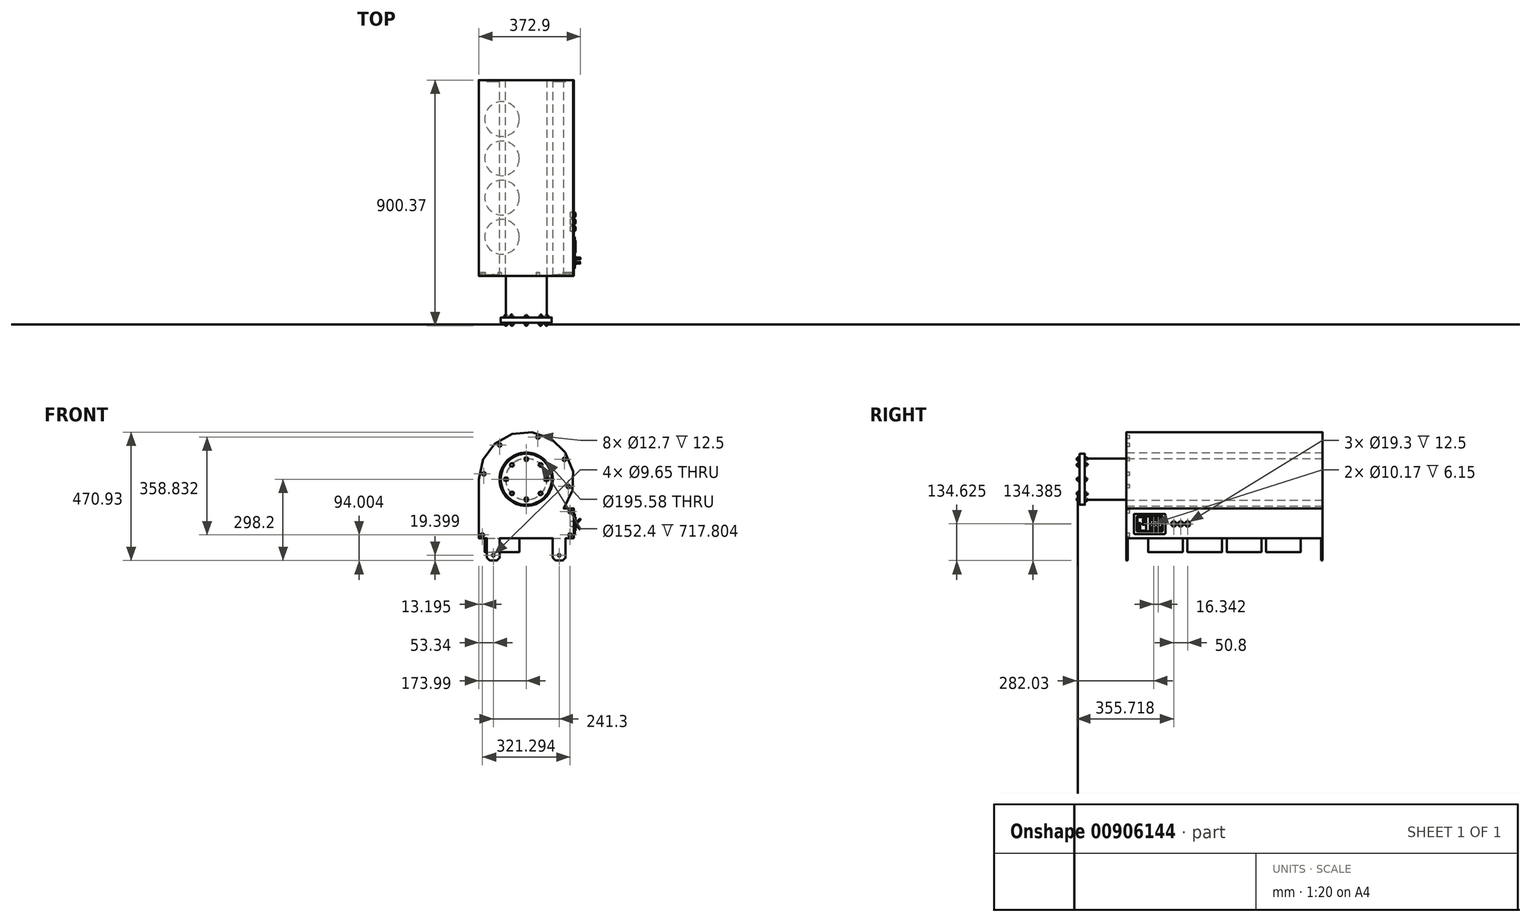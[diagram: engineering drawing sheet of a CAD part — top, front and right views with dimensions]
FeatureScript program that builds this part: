
annotation { "Feature Type Name" : "Feature", "Feature Type Description" : "" }
export const myFeature = defineFeature(function(context is Context, id is Id, definition is map)
    precondition{}
    {
        {
            var Q0;
            Q0=qCreatedBy(makeId("Front.planeOp"),FACE);
            var sketch = newSketch(context, id + "F0", { "sketchPlane" : qUnion([Q0])});
            skCircle(sketch, "E0", {"center": v(0, 0) * mm, "radius": 76.2 * mm});
            skCircle(sketch, "E1", {"center": v(0, 0) * mm, "radius": 97.8 * mm});
            skArc(sketch, "E2", {"start": v(137.14, -107.07) * mm, "mid": v(56.62, 164.52) * mm, "end": v(-174, 0) * mm});
            skLineSegment(sketch, "E3.top", {"start": v(-174, -216.3) * mm, "end": v(174, -216.3) * mm});
            skLineSegment(sketch, "E3.left", {"start": v(-174, -216.3) * mm, "end": v(-174, -216.3) * mm});
            skLineSegment(sketch, "E3.right", {"start": v(174, -107.07) * mm, "end": v(174, -216.3) * mm});
            skLineSegment(sketch, "E4", {"start": v(-174, 0) * mm, "end": v(-174, -216.3) * mm});
            skLineSegment(sketch, "E5.trimOffspring", {"start": v(137.14, -107.07) * mm, "end": v(174, -107.07) * mm});
            skLineSegment(sketch, "E6.bottom", {"start": v(96.9, -216.3) * mm, "end": v(144.4, -216.3) * mm});
            skLineSegment(sketch, "E6.top", {"start": v(96.9, -298.2) * mm, "end": v(144.4, -298.2) * mm});
            skLineSegment(sketch, "E6.left", {"start": v(96.9, -216.3) * mm, "end": v(96.9, -298.2) * mm});
            skLineSegment(sketch, "E6.right", {"start": v(144.4, -216.3) * mm, "end": v(144.4, -298.2) * mm});
            skLineSegment(sketch, "E7.bottom", {"start": v(-144.4, -216.3) * mm, "end": v(-96.9, -216.3) * mm});
            skLineSegment(sketch, "E7.top", {"start": v(-144.4, -298.2) * mm, "end": v(-96.9, -298.2) * mm});
            skLineSegment(sketch, "E7.left", {"start": v(-96.9, -216.3) * mm, "end": v(-96.9, -298.2) * mm});
            skLineSegment(sketch, "E7.right", {"start": v(-144.4, -216.3) * mm, "end": v(-144.4, -298.2) * mm});
            skCircle(sketch, "E8", {"center": v(-120.65, -278.8) * mm, "radius": 4.83 * mm});
            skPoint(sketch, "E8.centerSnap0", {"position": v(-120.65, -298.2) * mm});
            skCircle(sketch, "E9", {"center": v(120.65, -278.8) * mm, "radius": 4.83 * mm});
            skPoint(sketch, "E9.centerSnap0", {"position": v(120.65, -298.2) * mm});
            skSolve(sketch);
        }
        {
            var Q0;
            Q0=makeQuery(id+"F0.imprint","IMPRINT",FACE,{"disambiguationData":[TD([[makeQuery(id+"F0.imprint","IMPRINT",EDGE,{"derivedFrom":sQuery(id+"F0.wireOp",EDGE,"E1")}),-1.0]])]});
            extrude(context, id + "F1", {"entities" : qUnion([Q0]), "depth" : 717.8 * mm, "offsetDistance" : 25.4 * mm});
        }
        {
            var Q0;
            Q0=makeQuery(id+"F0.imprint","IMPRINT",FACE,{"disambiguationData":[TD([[makeQuery(id+"F0.imprint","IMPRINT",EDGE,{"derivedFrom":sQuery(id+"F0.wireOp",EDGE,"E0")}),-1.0]])]});
            extrude(context, id + "F2", {"entities" : qUnion([Q0]), "depth" : 717.8 * mm, "offsetDistance" : 25.4 * mm});
        }
        {
            var Q0;
            Q0=makeQuery(id+"F0.imprint","IMPRINT",FACE,{"disambiguationData":[TD([[makeQuery(id+"F0.imprint","IMPRINT",EDGE,{"derivedFrom":sQuery(id+"F0.wireOp",EDGE,"E7.top")}),1.0]])]});
            var Q1;
            Q1=makeQuery(id+"F0.imprint","IMPRINT",FACE,{"disambiguationData":[TD([[makeQuery(id+"F0.imprint","IMPRINT",EDGE,{"derivedFrom":sQuery(id+"F0.wireOp",EDGE,"E6.top")}),1.0]])]});
            extrude(context, id + "F3", {"entities" : qUnion([Q0, Q1]), "operationType" : NewBodyOperationType.ADD, "depth" : 5.08 * mm, "offsetDistance" : 25.4 * mm});
        }
        {
            var Q0;
            Q0=makeQuery(id+"F1.opExtrude","SWEPT_FACE",FACE,{"disambiguationData":[OSD([sQuery(id+"F0.wireOp",EDGE,"E3.top")])]});
            var sketch = newSketch(context, id + "F4", { "sketchPlane" : qUnion([Q0])});
            skCircle(sketch, "E10", {"center": v(-89.17, 143) * mm, "radius": 63.5 * mm});
            skCircle(sketch, "E11", {"center": v(-89.17, 286.94) * mm, "radius": 63.5 * mm});
            skCircle(sketch, "E12", {"center": v(-89.17, 430.87) * mm, "radius": 63.5 * mm});
            skCircle(sketch, "E13", {"center": v(-89.17, 574.8) * mm, "radius": 63.5 * mm});
            skLineSegment(sketch, "E14", {"start": v(-89.17, 0) * mm, "end": v(-89.17, 1107.64) * mm});
            skSolve(sketch);
        }
        {
            var Q0;
            {var subQ0=sQuery(id+"F4.wireOp",EDGE,"E14");var subQ1=sQuery(id+"F4.wireOp",EDGE,"E13");var subQ2=makeQuery(id+"F4.imprint","INTERSECT",VERTEX,{"disambiguationData":[OD(0.0)],"derivedFrom":[subQ1,subQ0]});Q0=makeQuery(id+"F4.imprint","IMPRINT",FACE,{"disambiguationData":[TD([[makeQuery(id+"F4.imprint","IMPRINT",EDGE,{"disambiguationData":[TD([[subQ2,-1.0]])],"derivedFrom":subQ1}),1.0]])]});}
            var Q1;
            {var subQ0=sQuery(id+"F4.wireOp",EDGE,"E14");var subQ1=sQuery(id+"F4.wireOp",EDGE,"E13");var subQ2=makeQuery(id+"F4.imprint","INTERSECT",VERTEX,{"disambiguationData":[OD(0.0)],"derivedFrom":[subQ1,subQ0]});Q1=makeQuery(id+"F4.imprint","IMPRINT",FACE,{"disambiguationData":[TD([[makeQuery(id+"F4.imprint","IMPRINT",EDGE,{"disambiguationData":[TD([[subQ2,1.0]])],"derivedFrom":subQ1}),1.0]])]});}
            var Q2;
            {var subQ0=sQuery(id+"F4.wireOp",EDGE,"E14");var subQ1=sQuery(id+"F4.wireOp",EDGE,"E12");var subQ2=makeQuery(id+"F4.imprint","INTERSECT",VERTEX,{"disambiguationData":[OD(0.0)],"derivedFrom":[subQ1,subQ0]});Q2=makeQuery(id+"F4.imprint","IMPRINT",FACE,{"disambiguationData":[TD([[makeQuery(id+"F4.imprint","IMPRINT",EDGE,{"disambiguationData":[TD([[subQ2,-1.0]])],"derivedFrom":subQ1}),1.0]])]});}
            var Q3;
            {var subQ0=sQuery(id+"F4.wireOp",EDGE,"E14");var subQ1=sQuery(id+"F4.wireOp",EDGE,"E12");var subQ2=makeQuery(id+"F4.imprint","INTERSECT",VERTEX,{"disambiguationData":[OD(0.0)],"derivedFrom":[subQ1,subQ0]});Q3=makeQuery(id+"F4.imprint","IMPRINT",FACE,{"disambiguationData":[TD([[makeQuery(id+"F4.imprint","IMPRINT",EDGE,{"disambiguationData":[TD([[subQ2,1.0]])],"derivedFrom":subQ1}),1.0]])]});}
            var Q4;
            {var subQ0=sQuery(id+"F4.wireOp",EDGE,"E14");var subQ1=sQuery(id+"F4.wireOp",EDGE,"E11");var subQ2=makeQuery(id+"F4.imprint","INTERSECT",VERTEX,{"disambiguationData":[OD(0.0)],"derivedFrom":[subQ1,subQ0]});Q4=makeQuery(id+"F4.imprint","IMPRINT",FACE,{"disambiguationData":[TD([[makeQuery(id+"F4.imprint","IMPRINT",EDGE,{"disambiguationData":[TD([[subQ2,-1.0]])],"derivedFrom":subQ1}),1.0]])]});}
            var Q5;
            {var subQ0=sQuery(id+"F4.wireOp",EDGE,"E14");var subQ1=sQuery(id+"F4.wireOp",EDGE,"E11");var subQ2=makeQuery(id+"F4.imprint","INTERSECT",VERTEX,{"disambiguationData":[OD(0.0)],"derivedFrom":[subQ1,subQ0]});Q5=makeQuery(id+"F4.imprint","IMPRINT",FACE,{"disambiguationData":[TD([[makeQuery(id+"F4.imprint","IMPRINT",EDGE,{"disambiguationData":[TD([[subQ2,1.0]])],"derivedFrom":subQ1}),1.0]])]});}
            var Q6;
            {var subQ0=sQuery(id+"F4.wireOp",EDGE,"E14");var subQ1=sQuery(id+"F4.wireOp",EDGE,"E10");var subQ2=makeQuery(id+"F4.imprint","INTERSECT",VERTEX,{"disambiguationData":[OD(0.0)],"derivedFrom":[subQ1,subQ0]});Q6=makeQuery(id+"F4.imprint","IMPRINT",FACE,{"disambiguationData":[TD([[makeQuery(id+"F4.imprint","IMPRINT",EDGE,{"disambiguationData":[TD([[subQ2,-1.0]])],"derivedFrom":subQ1}),1.0]])]});}
            var Q7;
            {var subQ0=sQuery(id+"F4.wireOp",EDGE,"E14");var subQ1=sQuery(id+"F4.wireOp",EDGE,"E10");var subQ2=makeQuery(id+"F4.imprint","INTERSECT",VERTEX,{"disambiguationData":[OD(0.0)],"derivedFrom":[subQ1,subQ0]});Q7=makeQuery(id+"F4.imprint","IMPRINT",FACE,{"disambiguationData":[TD([[makeQuery(id+"F4.imprint","IMPRINT",EDGE,{"disambiguationData":[TD([[subQ2,1.0]])],"derivedFrom":subQ1}),1.0]])]});}
            var Q8;
            Q8=makeQuery(id+"F1.opExtrude","SWEPT_FACE",FACE,{"disambiguationData":[OSD([sQuery(id+"F0.wireOp",EDGE,"E3.top")])]});
            extrude(context, id + "F5", {"entities" : qUnion([Q0, Q1, Q2, Q3, Q4, Q5, Q6, Q7]), "depth" : 50.8 * mm, "endBoundEntityFace" : qUnion([Q8]), "offsetDistance" : 127 * mm});
        }
        {
            var Q0;
            Q0=makeQuery(id+"F0.imprint","IMPRINT",FACE,{"disambiguationData":[TD([[makeQuery(id+"F0.imprint","IMPRINT",EDGE,{"derivedFrom":sQuery(id+"F0.wireOp",EDGE,"E6.top")}),1.0]])]});
            var Q1;
            Q1=makeQuery(id+"F0.imprint","IMPRINT",FACE,{"disambiguationData":[TD([[makeQuery(id+"F0.imprint","IMPRINT",EDGE,{"derivedFrom":sQuery(id+"F0.wireOp",EDGE,"E7.top")}),1.0]])]});
            extrude(context, id + "F6", {"entities" : qUnion([Q0, Q1]), "operationType" : NewBodyOperationType.ADD, "depth" : 717.8 * mm, "offsetDistance" : 25.4 * mm, "hasSecondDirection" : true, "secondDirectionOppositeDirection" : false, "secondDirectionDepth" : 712.72 * mm});
        }
        {
            var Q0;
            Q0=makeQuery(id+"F6.opExtrude","SWEPT_EDGE",EDGE,{"disambiguationData":[OSD([sQuery(id+"F0.wireOp",EDGE,"E6.top"),sQuery(id+"F0.wireOp",EDGE,"E6.right")])]});
            var Q1;
            Q1=makeQuery(id+"F6.opExtrude","SWEPT_EDGE",EDGE,{"disambiguationData":[OSD([sQuery(id+"F0.wireOp",EDGE,"E6.top"),sQuery(id+"F0.wireOp",EDGE,"E6.left")])]});
            var Q2;
            Q2=makeQuery(id+"F6.opExtrude","SWEPT_EDGE",EDGE,{"disambiguationData":[OSD([sQuery(id+"F0.wireOp",EDGE,"E3.top"),sQuery(id+"F0.wireOp",EDGE,"E6.right")])]});
            var Q3;
            Q3=makeQuery(id+"F6.opExtrude","SWEPT_EDGE",EDGE,{"disambiguationData":[OSD([sQuery(id+"F0.wireOp",EDGE,"E3.top"),sQuery(id+"F0.wireOp",EDGE,"E6.left")])]});
            var Q4;
            Q4=makeQuery(id+"F6.opExtrude","SWEPT_EDGE",EDGE,{"disambiguationData":[OSD([sQuery(id+"F0.wireOp",EDGE,"E3.top"),sQuery(id+"F0.wireOp",EDGE,"E7.right")])]});
            var Q5;
            Q5=makeQuery(id+"F6.opExtrude","SWEPT_EDGE",EDGE,{"disambiguationData":[OSD([sQuery(id+"F0.wireOp",EDGE,"E7.top"),sQuery(id+"F0.wireOp",EDGE,"E7.right")])]});
            var Q6;
            Q6=makeQuery(id+"F6.opExtrude","SWEPT_EDGE",EDGE,{"disambiguationData":[OSD([sQuery(id+"F0.wireOp",EDGE,"E7.top"),sQuery(id+"F0.wireOp",EDGE,"E7.left")])]});
            var Q7;
            Q7=makeQuery(id+"F6.opExtrude","SWEPT_EDGE",EDGE,{"disambiguationData":[OSD([sQuery(id+"F0.wireOp",EDGE,"E3.top"),sQuery(id+"F0.wireOp",EDGE,"E7.left")])]});
            var Q8;
            Q8=makeQuery(id+"F3.opExtrude","SWEPT_EDGE",EDGE,{"disambiguationData":[OSD([sQuery(id+"F0.wireOp",EDGE,"E7.top"),sQuery(id+"F0.wireOp",EDGE,"E7.right")])]});
            var Q9;
            Q9=makeQuery(id+"F3.opExtrude","SWEPT_EDGE",EDGE,{"disambiguationData":[OSD([sQuery(id+"F0.wireOp",EDGE,"E7.top"),sQuery(id+"F0.wireOp",EDGE,"E7.left")])]});
            var Q10;
            Q10=makeQuery(id+"F3.opExtrude","SWEPT_EDGE",EDGE,{"disambiguationData":[OSD([sQuery(id+"F0.wireOp",EDGE,"E3.top"),sQuery(id+"F0.wireOp",EDGE,"E7.right")])]});
            var Q11;
            Q11=makeQuery(id+"F3.opExtrude","SWEPT_EDGE",EDGE,{"disambiguationData":[OSD([sQuery(id+"F0.wireOp",EDGE,"E3.top"),sQuery(id+"F0.wireOp",EDGE,"E7.left")])]});
            var Q12;
            Q12=makeQuery(id+"F3.opExtrude","SWEPT_EDGE",EDGE,{"disambiguationData":[OSD([sQuery(id+"F0.wireOp",EDGE,"E6.top"),sQuery(id+"F0.wireOp",EDGE,"E6.left")])]});
            var Q13;
            Q13=makeQuery(id+"F3.opExtrude","SWEPT_EDGE",EDGE,{"disambiguationData":[OSD([sQuery(id+"F0.wireOp",EDGE,"E6.top"),sQuery(id+"F0.wireOp",EDGE,"E6.right")])]});
            var Q14;
            Q14=makeQuery(id+"F3.opExtrude","SWEPT_EDGE",EDGE,{"disambiguationData":[OSD([sQuery(id+"F0.wireOp",EDGE,"E3.top"),sQuery(id+"F0.wireOp",EDGE,"E6.right")])]});
            var Q15;
            Q15=makeQuery(id+"F3.opExtrude","SWEPT_EDGE",EDGE,{"disambiguationData":[OSD([sQuery(id+"F0.wireOp",EDGE,"E3.top"),sQuery(id+"F0.wireOp",EDGE,"E6.left")])]});
            chamfer(context, id + "F7", {"entities" : qUnion([Q0, Q1, Q2, Q3, Q4, Q5, Q6, Q7, Q8, Q9, Q10, Q11, Q12, Q13, Q14, Q15]), "width" : 10.16 * mm, "tangentPropagation" : true});
        }
        {
            var Q0;
            {var subQ0=sQuery(id+"F0.wireOp",EDGE,"E3.top");Q0=makeQuery(id+"F6.boolean.opBoolean","MERGE",FACE,{"derivedFrom":[makeQuery(id+"F1.opExtrude","CAP_FACE",FACE,{"disambiguationData":[OSD([sQuery(id+"F0.wireOp",EDGE,"E1"),sQuery(id+"F0.wireOp",EDGE,"E2"),subQ0,sQuery(id+"F0.wireOp",EDGE,"E3.right"),sQuery(id+"F0.wireOp",EDGE,"E4"),sQuery(id+"F0.wireOp",EDGE,"E5.trimOffspring")])],"isStart":false}),makeQuery(id+"F6.opExtrude","CAP_FACE",FACE,{"disambiguationData":[OSD([subQ0,sQuery(id+"F0.wireOp",EDGE,"E7.top"),sQuery(id+"F0.wireOp",EDGE,"E7.left"),sQuery(id+"F0.wireOp",EDGE,"E7.right"),sQuery(id+"F0.wireOp",EDGE,"E8")])],"isStart":false}),makeQuery(id+"F6.opExtrude","CAP_FACE",FACE,{"disambiguationData":[OSD([subQ0,sQuery(id+"F0.wireOp",EDGE,"E6.top"),sQuery(id+"F0.wireOp",EDGE,"E6.left"),sQuery(id+"F0.wireOp",EDGE,"E6.right"),sQuery(id+"F0.wireOp",EDGE,"E9")])],"isStart":false})]});}
            var sketch = newSketch(context, id + "F8", { "sketchPlane" : qUnion([Q0])});
            skCircle(sketch, "E15", {"center": v(0, 0) * mm, "radius": 75.2 * mm});
            skSolve(sketch);
        }
        {
            var Q0;
            Q0 = qSketchRegion(id + "F8", true);
            extrude(context, id + "F9", {"entities" : qUnion([Q0]), "depth" : 152.4 * mm, "offsetDistance" : 25.4 * mm});
        }
        {
            var Q0;
            Q0=makeQuery(id+"F9.opExtrude","CAP_FACE",FACE,{"disambiguationData":[OSD([sQuery(id+"F8.wireOp",EDGE,"E15")])],"isStart":false});
            var sketch = newSketch(context, id + "F10", { "sketchPlane" : qUnion([Q0])});
            skCircle(sketch, "E16", {"center": v(0, 0) * mm, "radius": 93.36 * mm});
            skSolve(sketch);
        }
        {
            var Q0;
            Q0 = qSketchRegion(id + "F10", true);
            extrude(context, id + "F11", {"entities" : qUnion([Q0]), "operationType" : NewBodyOperationType.ADD, "depth" : 19.05 * mm, "offsetDistance" : 25.4 * mm});
        }
        {
            var Q0;
            Q0=makeQuery(id+"F11.opExtrude","CAP_FACE",FACE,{"disambiguationData":[OSD([sQuery(id+"F10.wireOp",EDGE,"E16")])],"isStart":false});
            var sketch = newSketch(context, id + "F12", { "sketchPlane" : qUnion([Q0])});
            skLineSegment(sketch, "E17", {"start": v(0, 0) * mm, "end": v(0, 93.36) * mm, "construction": true});
            skCircle(sketch, "E18.cCircle", {"center": v(0, 74.1) * mm, "radius": 6.35 * mm, "construction": true});
            skLineSegment(sketch, "E18.0", {"start": v(6.35, 77.76) * mm, "end": v(6.35, 70.43) * mm});
            skLineSegment(sketch, "E18.1", {"start": v(6.35, 70.43) * mm, "end": v(0, 66.76) * mm});
            skLineSegment(sketch, "E18.2", {"start": v(0, 66.76) * mm, "end": v(-6.35, 70.43) * mm});
            skLineSegment(sketch, "E18.3", {"start": v(-6.35, 70.43) * mm, "end": v(-6.35, 77.76) * mm});
            skLineSegment(sketch, "E18.4", {"start": v(-6.35, 77.76) * mm, "end": v(0, 81.43) * mm});
            skLineSegment(sketch, "E18.5", {"start": v(0, 81.43) * mm, "end": v(6.35, 77.76) * mm});
            skPoint(sketch, "E18.0.midPoint", {"position": v(6.35, 74.1) * mm});
            skSolve(sketch);
        }
        {
            var Q0;
            Q0 = qSketchRegion(id + "F12", true);
            extrude(context, id + "F13", {"entities" : qUnion([Q0]), "depth" : 6.35 * mm, "offsetDistance" : 25.4 * mm});
        }
        {
            var Q0;
            Q0=makeQuery(id+"F13.opExtrude","CAP_FACE",FACE,{"disambiguationData":[OSD([sQuery(id+"F12.wireOp",EDGE,"E18.0"),sQuery(id+"F12.wireOp",EDGE,"E18.1"),sQuery(id+"F12.wireOp",EDGE,"E18.2"),sQuery(id+"F12.wireOp",EDGE,"E18.3"),sQuery(id+"F12.wireOp",EDGE,"E18.4"),sQuery(id+"F12.wireOp",EDGE,"E18.5")])],"isStart":false});
            var sketch = newSketch(context, id + "F14", { "sketchPlane" : qUnion([Q0])});
            skCircle(sketch, "E19", {"center": v(0, 74.1) * mm, "radius": 4.76 * mm});
            skSolve(sketch);
        }
        {
            var Q0;
            Q0 = qSketchRegion(id + "F14", true);
            extrude(context, id + "F15", {"entities" : qUnion([Q0]), "operationType" : NewBodyOperationType.ADD, "depth" : 4.76 * mm, "offsetDistance" : 25.4 * mm});
        }
        {
            var Q0;
            Q0=makeQuery(id+"F15.opExtrude","CAP_FACE",FACE,{"disambiguationData":[OSD([sQuery(id+"F14.wireOp",EDGE,"E19")])],"isStart":false});
            fillet(context, id + "F16", {"entities" : qUnion([Q0]), "radius" : 4.76 * mm, "tangentPropagation" : true, "rho" : 0.5, "crossSection" : FilletCrossSection.CONIC, "allowEdgeOverflow" : false});
        }
        {
            var Q0;
            Q0=makeQuery(id+"F11.opExtrude","CAP_EDGE",EDGE,{"disambiguationData":[OSD([sQuery(id+"F10.wireOp",EDGE,"E16")])],"isStart":false});
            var Q1;
            Q1=makeQuery(id+"F11.opExtrude","CAP_EDGE",EDGE,{"disambiguationData":[OSD([sQuery(id+"F10.wireOp",EDGE,"E16")])],"isStart":true});
            fillet(context, id + "F17", {"entities" : qUnion([Q0, Q1]), "radius" : 0.2 * mm, "tangentPropagation" : true, "allowEdgeOverflow" : false});
        }
        {
            var Q0;
            Q0=makeQuery(id+"F12.imprint","IMPRINT",FACE,{"disambiguationData":[TD([[makeQuery(id+"F12.imprint","IMPRINT",EDGE,{"derivedFrom":sQuery(id+"F12.wireOp",EDGE,"E18.0")}),1.0]])]});
            var Q1;
            Q1=makeQuery(id+"F11.opExtrude","CAP_FACE",FACE,{"disambiguationData":[OSD([sQuery(id+"F10.wireOp",EDGE,"E16")])],"isStart":true});
            cPlane(context, id + "F18", {"entities" : qUnion([Q0, Q1]), "cplaneType" : CPlaneType.MID_PLANE, "offset" : 25.4 * mm, "width" : 152.4 * mm, "height" : 152.4 * mm});
        }
        {
            var Q0;
            Q0=makeQuery(id+"F13.opExtrude","SWEPT_BODY",BODY,{"disambiguationData":[OSD([sQuery(id+"F12.wireOp",EDGE,"E18.0"),sQuery(id+"F12.wireOp",EDGE,"E18.1"),sQuery(id+"F12.wireOp",EDGE,"E18.2"),sQuery(id+"F12.wireOp",EDGE,"E18.3"),sQuery(id+"F12.wireOp",EDGE,"E18.4"),sQuery(id+"F12.wireOp",EDGE,"E18.5")])]});
            var Q1;
            Q1=qCreatedBy(id+"F18.planeOp",FACE);
            mirror(context, id + "F19", {"entities" : qUnion([Q0]), "mirrorPlane" : qUnion([Q1])});
        }
        {
            var Q0;
            Q0=sQuery(id+"F12.wireOp",EDGE,"E17");
            cPlane(context, id + "F20", {"entities" : qUnion([Q0]), "cplaneType" : CPlaneType.LINE_ANGLE, "offset" : 25.4 * mm, "angle" : 0 * degree, "width" : 152.4 * mm, "height" : 152.4 * mm});
        }
        {
            var Q0;
            Q0=qCreatedBy(id+"F20.planeOp",FACE);
            var sketch = newSketch(context, id + "F21", { "sketchPlane" : qUnion([Q0])});
            skLineSegment(sketch, "E20", {"start": v(-905.59, 0) * mm, "end": v(-759.23, 0) * mm, "construction": true});
            skSolve(sketch);
        }
        {
            var Q0;
            Q0=makeQuery(id+"F13.opExtrude","SWEPT_BODY",BODY,{"disambiguationData":[OSD([sQuery(id+"F12.wireOp",EDGE,"E18.0"),sQuery(id+"F12.wireOp",EDGE,"E18.1"),sQuery(id+"F12.wireOp",EDGE,"E18.2"),sQuery(id+"F12.wireOp",EDGE,"E18.3"),sQuery(id+"F12.wireOp",EDGE,"E18.4"),sQuery(id+"F12.wireOp",EDGE,"E18.5")])]});
            var Q1;
            Q1=makeQuery(id+"F19.opPattern","COPY",BODY,{"derivedFrom":makeQuery(id+"F13.opExtrude","SWEPT_BODY",BODY,{"disambiguationData":[OSD([sQuery(id+"F12.wireOp",EDGE,"E18.0"),sQuery(id+"F12.wireOp",EDGE,"E18.1"),sQuery(id+"F12.wireOp",EDGE,"E18.2"),sQuery(id+"F12.wireOp",EDGE,"E18.3"),sQuery(id+"F12.wireOp",EDGE,"E18.4"),sQuery(id+"F12.wireOp",EDGE,"E18.5")])]}),"instanceName":"1"});
            var Q2;
            Q2=sQuery(id+"F21.wireOp",EDGE,"E20");
            circularPattern(context, id + "F22", {"entities" : qUnion([Q0, Q1]), "axis" : qUnion([Q2]), "angle" : 360 * degree, "instanceCount" : 8, "equalSpace" : true});
        }
        {
            var Q0;
            Q0=makeQuery(id+"F1.opExtrude","SWEPT_FACE",FACE,{"disambiguationData":[OSD([sQuery(id+"F0.wireOp",EDGE,"E3.right")])]});
            var sketch = newSketch(context, id + "F23", { "sketchPlane" : qUnion([Q0])});
            skLineSegment(sketch, "E21.bottom", {"start": v(-678.44, -136.9) * mm, "end": v(-587.4, -136.9) * mm});
            skLineSegment(sketch, "E21.top", {"start": v(-678.44, -190.72) * mm, "end": v(-587.4, -190.72) * mm});
            skLineSegment(sketch, "E21.left", {"start": v(-680.44, -138.9) * mm, "end": v(-680.44, -188.72) * mm});
            skLineSegment(sketch, "E21.right", {"start": v(-585.4, -138.9) * mm, "end": v(-585.4, -188.72) * mm});
            skLineSegment(sketch, "E22", {"start": v(-680.44, -190.72) * mm, "end": v(-585.4, -136.9) * mm, "construction": true});
            skLineSegment(sketch, "E23.bottom", {"start": v(-687.44, -126.9) * mm, "end": v(-578.4, -126.9) * mm});
            skLineSegment(sketch, "E23.top", {"start": v(-687.44, -200.72) * mm, "end": v(-578.4, -200.72) * mm});
            skLineSegment(sketch, "E23.left", {"start": v(-690.44, -129.9) * mm, "end": v(-690.44, -197.72) * mm});
            skLineSegment(sketch, "E23.right", {"start": v(-575.4, -129.9) * mm, "end": v(-575.4, -197.72) * mm});
            skLineSegment(sketch, "E24", {"start": v(-632.92, -190.72) * mm, "end": v(-632.92, -200.72) * mm, "construction": true});
            skLineSegment(sketch, "E25", {"start": v(-575.4, -163.81) * mm, "end": v(-585.4, -163.81) * mm, "construction": true});
            skPoint(sketch, "E26.visualSharp", {"position": v(-680.44, -136.9) * mm});
            skArc(sketch, "E26.filletArc", {"start": v(-678.44, -136.9) * mm, "mid": v(-679.86, -137.5) * mm, "end": v(-680.44, -138.9) * mm});
            skPoint(sketch, "E27.visualSharp", {"position": v(-585.4, -136.9) * mm});
            skArc(sketch, "E27.filletArc", {"start": v(-585.4, -138.9) * mm, "mid": v(-585.99, -137.5) * mm, "end": v(-587.4, -136.9) * mm});
            skPoint(sketch, "E28.visualSharp", {"position": v(-585.4, -190.72) * mm});
            skArc(sketch, "E28.filletArc", {"start": v(-587.4, -190.72) * mm, "mid": v(-585.99, -190.14) * mm, "end": v(-585.4, -188.72) * mm});
            skPoint(sketch, "E29.visualSharp", {"position": v(-680.44, -190.72) * mm});
            skArc(sketch, "E29.filletArc", {"start": v(-680.44, -188.72) * mm, "mid": v(-679.86, -190.14) * mm, "end": v(-678.44, -190.72) * mm});
            skPoint(sketch, "E30.visualSharp", {"position": v(-690.44, -126.9) * mm});
            skArc(sketch, "E30.filletArc", {"start": v(-687.44, -126.9) * mm, "mid": v(-689.56, -127.78) * mm, "end": v(-690.44, -129.9) * mm});
            skPoint(sketch, "E31.visualSharp", {"position": v(-575.4, -126.9) * mm});
            skArc(sketch, "E31.filletArc", {"start": v(-575.4, -129.9) * mm, "mid": v(-576.28, -127.78) * mm, "end": v(-578.4, -126.9) * mm});
            skPoint(sketch, "E32.visualSharp", {"position": v(-575.4, -200.72) * mm});
            skArc(sketch, "E32.filletArc", {"start": v(-578.4, -200.72) * mm, "mid": v(-576.28, -199.85) * mm, "end": v(-575.4, -197.72) * mm});
            skPoint(sketch, "E33.visualSharp", {"position": v(-690.44, -200.72) * mm});
            skArc(sketch, "E33.filletArc", {"start": v(-690.44, -197.72) * mm, "mid": v(-689.56, -199.85) * mm, "end": v(-687.44, -200.72) * mm});
            skSolve(sketch);
        }
        {
            var Q0;
            Q0 = qSketchRegion(id + "F23", true);
            extrude(context, id + "F24", {"entities" : qUnion([Q0]), "depth" : 4 * mm, "offsetDistance" : 25.4 * mm});
        }
        {
            var Q0;
            Q0=makeQuery(id+"F24.opExtrude","CAP_FACE",FACE,{"disambiguationData":[OSD([sQuery(id+"F23.wireOp",EDGE,"E21.bottom"),sQuery(id+"F23.wireOp",EDGE,"E21.top"),sQuery(id+"F23.wireOp",EDGE,"E21.left"),sQuery(id+"F23.wireOp",EDGE,"E21.right"),sQuery(id+"F23.wireOp",EDGE,"E23.bottom"),sQuery(id+"F23.wireOp",EDGE,"E23.top"),sQuery(id+"F23.wireOp",EDGE,"E23.left"),sQuery(id+"F23.wireOp",EDGE,"E23.right"),sQuery(id+"F23.wireOp",EDGE,"E26.filletArc"),sQuery(id+"F23.wireOp",EDGE,"E27.filletArc"),sQuery(id+"F23.wireOp",EDGE,"E28.filletArc"),sQuery(id+"F23.wireOp",EDGE,"E29.filletArc"),sQuery(id+"F23.wireOp",EDGE,"E30.filletArc"),sQuery(id+"F23.wireOp",EDGE,"E31.filletArc"),sQuery(id+"F23.wireOp",EDGE,"E32.filletArc"),sQuery(id+"F23.wireOp",EDGE,"E33.filletArc")])],"isStart":false});
            fillet(context, id + "F25", {"entities" : qUnion([Q0]), "radius" : 1 * mm, "tangentPropagation" : true, "allowEdgeOverflow" : false});
        }
        {
            var Q0;
            {var subQ0=sQuery(id+"F0.wireOp",EDGE,"E3.top");Q0=makeQuery(id+"F6.boolean.opBoolean","MERGE",FACE,{"derivedFrom":[makeQuery(id+"F1.opExtrude","CAP_FACE",FACE,{"disambiguationData":[OSD([sQuery(id+"F0.wireOp",EDGE,"E1"),sQuery(id+"F0.wireOp",EDGE,"E2"),subQ0,sQuery(id+"F0.wireOp",EDGE,"E3.right"),sQuery(id+"F0.wireOp",EDGE,"E4"),sQuery(id+"F0.wireOp",EDGE,"E5.trimOffspring")])],"isStart":false}),makeQuery(id+"F6.opExtrude","CAP_FACE",FACE,{"disambiguationData":[OSD([subQ0,sQuery(id+"F0.wireOp",EDGE,"E7.top"),sQuery(id+"F0.wireOp",EDGE,"E7.left"),sQuery(id+"F0.wireOp",EDGE,"E7.right"),sQuery(id+"F0.wireOp",EDGE,"E8")])],"isStart":false}),makeQuery(id+"F6.opExtrude","CAP_FACE",FACE,{"disambiguationData":[OSD([subQ0,sQuery(id+"F0.wireOp",EDGE,"E6.top"),sQuery(id+"F0.wireOp",EDGE,"E6.left"),sQuery(id+"F0.wireOp",EDGE,"E6.right"),sQuery(id+"F0.wireOp",EDGE,"E9")])],"isStart":false})]});}
            var sketch = newSketch(context, id + "F26", { "sketchPlane" : qUnion([Q0])});
            skCircle(sketch, "E34", {"center": v(-97.37, 125.44) * mm, "radius": 6.35 * mm});
            skCircle(sketch, "E35", {"center": v(42.68, 154.64) * mm, "radius": 6.35 * mm});
            skCircle(sketch, "E36", {"center": v(139.9, 72.94) * mm, "radius": 6.35 * mm});
            skCircle(sketch, "E37", {"center": v(-155.38, 19.68) * mm, "radius": 6.35 * mm});
            skCircle(sketch, "E38", {"center": v(-160.8, -204.2) * mm, "radius": 6.35 * mm});
            skCircle(sketch, "E39", {"center": v(160.5, -204.2) * mm, "radius": 6.35 * mm});
            skCircle(sketch, "E40", {"center": v(160.5, -118.6) * mm, "radius": 6.35 * mm});
            skCircle(sketch, "E41", {"center": v(154.01, -26.43) * mm, "radius": 6.35 * mm});
            skSolve(sketch);
        }
        {
            var Q0;
            Q0 = qSketchRegion(id + "F26", true);
            extrude(context, id + "F27", {"entities" : qUnion([Q0]), "operationType" : NewBodyOperationType.REMOVE, "oppositeDirection" : true, "depth" : 12.7 * mm, "offsetDistance" : 25.4 * mm});
        }
        {
            var Q0;
            {var subQ0=sQuery(id+"F0.wireOp",EDGE,"E3.top");Q0=makeQuery(id+"F6.boolean.opBoolean","MERGE",FACE,{"derivedFrom":[makeQuery(id+"F1.opExtrude","CAP_FACE",FACE,{"disambiguationData":[OSD([sQuery(id+"F0.wireOp",EDGE,"E1"),sQuery(id+"F0.wireOp",EDGE,"E2"),subQ0,sQuery(id+"F0.wireOp",EDGE,"E3.right"),sQuery(id+"F0.wireOp",EDGE,"E4"),sQuery(id+"F0.wireOp",EDGE,"E5.trimOffspring")])],"isStart":false}),makeQuery(id+"F6.opExtrude","CAP_FACE",FACE,{"disambiguationData":[OSD([subQ0,sQuery(id+"F0.wireOp",EDGE,"E7.top"),sQuery(id+"F0.wireOp",EDGE,"E7.left"),sQuery(id+"F0.wireOp",EDGE,"E7.right"),sQuery(id+"F0.wireOp",EDGE,"E8")])],"isStart":false}),makeQuery(id+"F6.opExtrude","CAP_FACE",FACE,{"disambiguationData":[OSD([subQ0,sQuery(id+"F0.wireOp",EDGE,"E6.top"),sQuery(id+"F0.wireOp",EDGE,"E6.left"),sQuery(id+"F0.wireOp",EDGE,"E6.right"),sQuery(id+"F0.wireOp",EDGE,"E9")])],"isStart":false})]});}
            var sketch = newSketch(context, id + "F28", { "sketchPlane" : qUnion([Q0])});
            skCircle(sketch, "E42", {"center": v(-160.8, -204.2) * mm, "radius": 5.72 * mm});
            skCircle(sketch, "E43", {"center": v(-155.38, 19.68) * mm, "radius": 5.72 * mm});
            skCircle(sketch, "E44", {"center": v(-97.37, 125.44) * mm, "radius": 5.72 * mm});
            skCircle(sketch, "E45", {"center": v(42.68, 154.64) * mm, "radius": 5.72 * mm});
            skCircle(sketch, "E46", {"center": v(139.9, 72.94) * mm, "radius": 5.72 * mm});
            skCircle(sketch, "E47", {"center": v(154.01, -26.43) * mm, "radius": 5.72 * mm});
            skCircle(sketch, "E48", {"center": v(160.5, -118.6) * mm, "radius": 5.72 * mm});
            skCircle(sketch, "E49", {"center": v(160.5, -204.2) * mm, "radius": 5.72 * mm});
            skSolve(sketch);
        }
        {
            var Q0;
            Q0 = qSketchRegion(id + "F28", true);
            extrude(context, id + "F29", {"entities" : qUnion([Q0]), "oppositeDirection" : true, "depth" : 11.43 * mm, "offsetDistance" : 25.4 * mm});
        }
        {
            var Q0;
            Q0=makeQuery(id+"F1.opExtrude","SWEPT_FACE",FACE,{"disambiguationData":[OSD([sQuery(id+"F0.wireOp",EDGE,"E3.right")])]});
            var sketch = newSketch(context, id + "F30", { "sketchPlane" : qUnion([Q0])});
            skLineSegment(sketch, "E50.bottom", {"start": v(-677.9, -139.44) * mm, "end": v(-646.15, -139.44) * mm});
            skLineSegment(sketch, "E50.top", {"start": v(-677.9, -188.18) * mm, "end": v(-646.15, -188.18) * mm});
            skLineSegment(sketch, "E50.left", {"start": v(-677.9, -139.44) * mm, "end": v(-677.9, -188.18) * mm});
            skLineSegment(sketch, "E50.right", {"start": v(-646.15, -139.44) * mm, "end": v(-646.15, -188.18) * mm});
            skLineSegment(sketch, "E51.bottom", {"start": v(-632.4, -139.44) * mm, "end": v(-587.94, -139.44) * mm});
            skLineSegment(sketch, "E51.top", {"start": v(-632.4, -188.18) * mm, "end": v(-587.94, -188.18) * mm});
            skLineSegment(sketch, "E51.left", {"start": v(-632.4, -139.44) * mm, "end": v(-632.4, -188.18) * mm});
            skLineSegment(sketch, "E51.right", {"start": v(-587.94, -139.44) * mm, "end": v(-587.94, -188.18) * mm});
            skLineSegment(sketch, "E52.bottom", {"start": v(-627.46, -141.9) * mm, "end": v(-619.72, -141.9) * mm});
            skLineSegment(sketch, "E52.top", {"start": v(-627.46, -150.67) * mm, "end": v(-619.72, -150.67) * mm});
            skLineSegment(sketch, "E52.left", {"start": v(-627.46, -141.9) * mm, "end": v(-627.46, -150.67) * mm});
            skLineSegment(sketch, "E52.right", {"start": v(-619.72, -141.9) * mm, "end": v(-619.72, -150.67) * mm});
            skLineSegment(sketch, "E53.bottom", {"start": v(-613.7, -141.9) * mm, "end": v(-605.95, -141.9) * mm});
            skLineSegment(sketch, "E53.top", {"start": v(-613.7, -150.67) * mm, "end": v(-605.95, -150.67) * mm});
            skLineSegment(sketch, "E53.left", {"start": v(-613.7, -141.9) * mm, "end": v(-613.7, -150.67) * mm});
            skLineSegment(sketch, "E53.right", {"start": v(-605.95, -141.9) * mm, "end": v(-605.95, -150.67) * mm});
            skLineSegment(sketch, "E54.bottom", {"start": v(-600.28, -141.9) * mm, "end": v(-592.54, -141.9) * mm});
            skLineSegment(sketch, "E54.top", {"start": v(-600.28, -150.67) * mm, "end": v(-592.54, -150.67) * mm});
            skLineSegment(sketch, "E54.left", {"start": v(-600.28, -141.9) * mm, "end": v(-600.28, -150.67) * mm});
            skLineSegment(sketch, "E54.right", {"start": v(-592.54, -141.9) * mm, "end": v(-592.54, -150.67) * mm});
            skLineSegment(sketch, "E55.bottom", {"start": v(-627.46, -176.13) * mm, "end": v(-619.72, -176.13) * mm});
            skLineSegment(sketch, "E55.top", {"start": v(-627.46, -184.9) * mm, "end": v(-619.72, -184.9) * mm});
            skLineSegment(sketch, "E55.left", {"start": v(-627.46, -176.13) * mm, "end": v(-627.46, -184.9) * mm});
            skLineSegment(sketch, "E55.right", {"start": v(-619.72, -176.13) * mm, "end": v(-619.72, -184.9) * mm});
            skLineSegment(sketch, "E56.bottom", {"start": v(-613.7, -176.13) * mm, "end": v(-605.95, -176.13) * mm});
            skLineSegment(sketch, "E56.top", {"start": v(-613.7, -184.9) * mm, "end": v(-605.95, -184.9) * mm});
            skLineSegment(sketch, "E56.left", {"start": v(-613.7, -176.13) * mm, "end": v(-613.7, -184.9) * mm});
            skLineSegment(sketch, "E56.right", {"start": v(-605.95, -176.13) * mm, "end": v(-605.95, -184.9) * mm});
            skLineSegment(sketch, "E57.bottom", {"start": v(-600.28, -176.13) * mm, "end": v(-592.54, -176.13) * mm});
            skLineSegment(sketch, "E57.top", {"start": v(-600.28, -184.9) * mm, "end": v(-592.54, -184.9) * mm});
            skLineSegment(sketch, "E57.left", {"start": v(-600.28, -176.13) * mm, "end": v(-600.28, -184.9) * mm});
            skLineSegment(sketch, "E57.right", {"start": v(-592.54, -176.13) * mm, "end": v(-592.54, -184.9) * mm});
            skCircle(sketch, "E58", {"center": v(-618.34, -163.57) * mm, "radius": 5.09 * mm});
            skCircle(sketch, "E59", {"center": v(-602, -163.57) * mm, "radius": 5.09 * mm});
            skLineSegment(sketch, "E60.bottom", {"start": v(-673.14, -160.52) * mm, "end": v(-666.79, -160.52) * mm});
            skLineSegment(sketch, "E60.top", {"start": v(-673.14, -166.87) * mm, "end": v(-666.79, -166.87) * mm});
            skLineSegment(sketch, "E60.left", {"start": v(-673.14, -160.52) * mm, "end": v(-673.14, -166.87) * mm});
            skLineSegment(sketch, "E60.right", {"start": v(-666.79, -160.52) * mm, "end": v(-666.79, -166.87) * mm});
            skLineSegment(sketch, "E61.bottom", {"start": v(-657.26, -160.57) * mm, "end": v(-650.91, -160.57) * mm});
            skLineSegment(sketch, "E61.top", {"start": v(-657.26, -166.92) * mm, "end": v(-650.91, -166.92) * mm});
            skLineSegment(sketch, "E61.left", {"start": v(-657.26, -160.57) * mm, "end": v(-657.26, -166.92) * mm});
            skLineSegment(sketch, "E61.right", {"start": v(-650.91, -160.57) * mm, "end": v(-650.91, -166.92) * mm});
            skPoint(sketch, "E62", {"position": v(-646.15, -163.81) * mm});
            skPoint(sketch, "E63", {"position": v(-650.91, -163.75) * mm});
            skPoint(sketch, "E64", {"position": v(-666.79, -163.7) * mm});
            skPoint(sketch, "E65", {"position": v(-657.26, -163.75) * mm});
            skPoint(sketch, "E66", {"position": v(-662.03, -139.44) * mm});
            skLineSegment(sketch, "E67", {"start": v(-666.79, -163.7) * mm, "end": v(-657.26, -163.75) * mm, "construction": true});
            skPoint(sketch, "E68", {"position": v(-662.03, -163.72) * mm});
            skSolve(sketch);
        }
        {
            var Q0;
            Q0 = qSketchRegion(id + "F30", true);
            extrude(context, id + "F31", {"entities" : qUnion([Q0]), "operationType" : NewBodyOperationType.ADD, "depth" : 6.35 * mm, "offsetDistance" : 25.4 * mm});
        }
        {
            var Q0;
            Q0=makeQuery(id+"F31.opExtrude","SWEPT_FACE",FACE,{"disambiguationData":[OSD([sQuery(id+"F30.wireOp",EDGE,"E60.right")])]});
            cPlane(context, id + "F32", {"entities" : qUnion([Q0]), "cplaneType" : CPlaneType.OFFSET, "offset" : 0.25 * mm, "width" : 152.4 * mm, "height" : 152.4 * mm});
        }
        {
            var Q0;
            Q0=qCreatedBy(id+"F32.planeOp",FACE);
            var sketch = newSketch(context, id + "F33", { "sketchPlane" : qUnion([Q0])});
            skLineSegment(sketch, "E69", {"start": v(180.34, -166.61) * mm, "end": v(194.02, -182.51) * mm});
            skLineSegment(sketch, "E70", {"start": v(180.34, -160.77) * mm, "end": v(196.9, -180.03) * mm});
            skArc(sketch, "E71", {"start": v(194.02, -182.51) * mm, "mid": v(196.7, -182.71) * mm, "end": v(196.9, -180.03) * mm});
            skLineSegment(sketch, "E72", {"start": v(196.9, -180.03) * mm, "end": v(194.02, -182.51) * mm, "construction": true});
            skLineSegment(sketch, "E73", {"start": v(180.34, -166.61) * mm, "end": v(177.94, -166.61) * mm});
            skLineSegment(sketch, "E74", {"start": v(177.94, -166.61) * mm, "end": v(177.94, -160.77) * mm});
            skLineSegment(sketch, "E75", {"start": v(177.94, -160.77) * mm, "end": v(180.34, -160.77) * mm});
            skSolve(sketch);
        }
        {
            var Q0;
            Q0 = qSketchRegion(id + "F33", true);
            extrude(context, id + "F34", {"entities" : qUnion([Q0]), "depth" : 5.84 * mm, "offsetDistance" : 25.4 * mm});
        }
        {
            var Q0;
            Q0=makeQuery(id+"F31.opExtrude","SWEPT_FACE",FACE,{"disambiguationData":[OSD([sQuery(id+"F30.wireOp",EDGE,"E61.right")])]});
            cPlane(context, id + "F35", {"entities" : qUnion([Q0]), "cplaneType" : CPlaneType.OFFSET, "offset" : 0.25 * mm, "width" : 152.4 * mm, "height" : 152.4 * mm});
        }
        {
            var Q0;
            Q0=qCreatedBy(id+"F35.planeOp",FACE);
            var sketch = newSketch(context, id + "F36", { "sketchPlane" : qUnion([Q0])});
            skLineSegment(sketch, "E76", {"start": v(180.34, -166.61) * mm, "end": v(198.3, -148.65) * mm});
            skLineSegment(sketch, "E77", {"start": v(180.34, -160.77) * mm, "end": v(195.38, -145.73) * mm});
            skLineSegment(sketch, "E78", {"start": v(195.38, -145.73) * mm, "end": v(198.3, -148.65) * mm, "construction": true});
            skArc(sketch, "E79", {"start": v(198.3, -148.65) * mm, "mid": v(198.3, -145.73) * mm, "end": v(195.38, -145.73) * mm});
            skLineSegment(sketch, "E80", {"start": v(180.34, -160.77) * mm, "end": v(177.94, -160.77) * mm});
            skLineSegment(sketch, "E81", {"start": v(177.94, -160.77) * mm, "end": v(177.94, -166.61) * mm});
            skLineSegment(sketch, "E82", {"start": v(177.94, -166.61) * mm, "end": v(180.34, -166.61) * mm});
            skSolve(sketch);
        }
        {
            var Q0;
            Q0 = qSketchRegion(id + "F36", true);
            extrude(context, id + "F37", {"entities" : qUnion([Q0]), "depth" : 5.84 * mm, "offsetDistance" : 25.4 * mm});
        }
        {
            var Q0;
            {var subQ0=sQuery(id+"F0.wireOp",EDGE,"E3.top");Q0=makeQuery(id+"F6.boolean.opBoolean","MERGE",FACE,{"derivedFrom":[makeQuery(id+"F1.opExtrude","CAP_FACE",FACE,{"disambiguationData":[OSD([sQuery(id+"F0.wireOp",EDGE,"E1"),sQuery(id+"F0.wireOp",EDGE,"E2"),subQ0,sQuery(id+"F0.wireOp",EDGE,"E3.right"),sQuery(id+"F0.wireOp",EDGE,"E4"),sQuery(id+"F0.wireOp",EDGE,"E5.trimOffspring")])],"isStart":false}),makeQuery(id+"F6.opExtrude","CAP_FACE",FACE,{"disambiguationData":[OSD([subQ0,sQuery(id+"F0.wireOp",EDGE,"E7.top"),sQuery(id+"F0.wireOp",EDGE,"E7.left"),sQuery(id+"F0.wireOp",EDGE,"E7.right"),sQuery(id+"F0.wireOp",EDGE,"E8")])],"isStart":false}),makeQuery(id+"F6.opExtrude","CAP_FACE",FACE,{"disambiguationData":[OSD([subQ0,sQuery(id+"F0.wireOp",EDGE,"E6.top"),sQuery(id+"F0.wireOp",EDGE,"E6.left"),sQuery(id+"F0.wireOp",EDGE,"E6.right"),sQuery(id+"F0.wireOp",EDGE,"E9")])],"isStart":false})]});}
            var sketch = newSketch(context, id + "F38", { "sketchPlane" : qUnion([Q0])});
            skLineSegment(sketch, "E83", {"start": v(137.14, -107.07) * mm, "end": v(169, -41.38) * mm});
            skLineSegment(sketch, "E84", {"start": v(169, -41.38) * mm, "end": v(171.1, 31.59) * mm});
            skLineSegment(sketch, "E85", {"start": v(171.1, 31.59) * mm, "end": v(143.08, 99) * mm});
            skLineSegment(sketch, "E86", {"start": v(143.08, 99) * mm, "end": v(89.87, 148.98) * mm});
            skLineSegment(sketch, "E87", {"start": v(89.87, 148.98) * mm, "end": v(20.84, 172.74) * mm});
            skLineSegment(sketch, "E88", {"start": v(20.84, 172.74) * mm, "end": v(-51.86, 166.08) * mm});
            skLineSegment(sketch, "E89", {"start": v(-51.86, 166.08) * mm, "end": v(-115.43, 130.19) * mm});
            skLineSegment(sketch, "E90", {"start": v(-115.43, 130.19) * mm, "end": v(-158.67, 71.38) * mm});
            skLineSegment(sketch, "E91", {"start": v(-158.67, 71.38) * mm, "end": v(-174, 0) * mm});
            skLineSegment(sketch, "E92", {"start": v(137.14, -107.07) * mm, "end": v(271.94, 21.27) * mm});
            skLineSegment(sketch, "E93", {"start": v(271.94, 21.27) * mm, "end": v(36.49, 229.68) * mm});
            skLineSegment(sketch, "E94", {"start": v(36.49, 229.68) * mm, "end": v(-221.01, 125.83) * mm});
            skLineSegment(sketch, "E95", {"start": v(-221.01, 125.83) * mm, "end": v(-174, 0) * mm});
            skSolve(sketch);
        }
        {
            var Q0;
            Q0 = qSketchRegion(id + "F38", true);
            extrude(context, id + "F39", {"entities" : qUnion([Q0]), "operationType" : NewBodyOperationType.REMOVE, "endBound" : BoundingType.THROUGH_ALL, "oppositeDirection" : true, "depth" : 25.4 * mm, "offsetDistance" : 25.4 * mm});
        }
        {
            var Q0;
            {var subQ4=sQuery(id+"F0.wireOp",EDGE,"E3.top");var subQ11=sQuery(id+"F0.wireOp",EDGE,"E3.right");Q0=makeQuery(id+"F31.boolean.opBoolean","SPLIT",FACE,{"disambiguationData":[TD([makeQuery(id+"F1.opExtrude","SWEPT_FACE",FACE,{"disambiguationData":[OSD([subQ4])]})])],"derivedFrom":makeQuery(id+"F1.opExtrude","SWEPT_FACE",FACE,{"disambiguationData":[OSD([subQ11])]})});}
            var sketch = newSketch(context, id + "F40", { "sketchPlane" : qUnion([Q0])});
            skCircle(sketch, "E96", {"center": v(-544.65, -163.81) * mm, "radius": 9.65 * mm});
            skCircle(sketch, "E97", {"center": v(-519.25, -163.81) * mm, "radius": 9.65 * mm});
            skCircle(sketch, "E98", {"center": v(-493.85, -163.81) * mm, "radius": 9.65 * mm});
            skLineSegment(sketch, "E99", {"start": v(-544.65, -163.81) * mm, "end": v(-519.25, -163.81) * mm, "construction": true});
            skLineSegment(sketch, "E100", {"start": v(-519.25, -163.81) * mm, "end": v(-493.85, -163.81) * mm, "construction": true});
            skSolve(sketch);
        }
        {
            var Q0;
            Q0 = qSketchRegion(id + "F40", true);
            extrude(context, id + "F41", {"entities" : qUnion([Q0]), "operationType" : NewBodyOperationType.REMOVE, "oppositeDirection" : true, "depth" : 12.7 * mm, "offsetDistance" : 25.4 * mm});
        }
        {
            var Q0;
            Q0=makeQuery(id+"F41.boolean.opBoolean","COPY",FACE,{"derivedFrom":makeQuery(id+"F41.opExtrude","CAP_FACE",FACE,{"disambiguationData":[OSD([sQuery(id+"F40.wireOp",EDGE,"E96")])],"isStart":false})});
            cPlane(context, id + "F42", {"entities" : qUnion([Q0]), "cplaneType" : CPlaneType.OFFSET, "offset" : 0.25 * mm, "width" : 152.4 * mm, "height" : 152.4 * mm});
        }
        {
            var Q0;
            Q0=qCreatedBy(id+"F42.planeOp",FACE);
            var sketch = newSketch(context, id + "F43", { "sketchPlane" : qUnion([Q0])});
            skCircle(sketch, "E101", {"center": v(-544.65, -163.81) * mm, "radius": 9.14 * mm});
            skCircle(sketch, "E102", {"center": v(-519.25, -163.81) * mm, "radius": 9.14 * mm});
            skCircle(sketch, "E103", {"center": v(-493.85, -163.81) * mm, "radius": 9.14 * mm});
            skSolve(sketch);
        }
        {
            var Q0;
            Q0 = qSketchRegion(id + "F43", true);
            extrude(context, id + "F44", {"entities" : qUnion([Q0]), "depth" : 19.05 * mm, "offsetDistance" : 25.4 * mm});
        }
        {
            var Q0;
            Q0=makeQuery(id+"F44.opExtrude","CAP_EDGE",EDGE,{"disambiguationData":[OSD([sQuery(id+"F43.wireOp",EDGE,"E101")])],"isStart":false});
            var Q1;
            Q1=makeQuery(id+"F44.opExtrude","CAP_EDGE",EDGE,{"disambiguationData":[OSD([sQuery(id+"F43.wireOp",EDGE,"E102")])],"isStart":false});
            var Q2;
            Q2=makeQuery(id+"F44.opExtrude","CAP_EDGE",EDGE,{"disambiguationData":[OSD([sQuery(id+"F43.wireOp",EDGE,"E103")])],"isStart":false});
            fillet(context, id + "F45", {"entities" : qUnion([Q0, Q1, Q2]), "radius" : 5.08 * mm, "tangentPropagation" : true, "allowEdgeOverflow" : false});
        }
        {
            var Q0;
            Q0=makeQuery(id+"F39.boolean.opBoolean","COPY",EDGE,{"derivedFrom":makeQuery(id+"F39.opExtrude","CAP_EDGE",EDGE,{"disambiguationData":[OSD([sQuery(id+"F38.wireOp",EDGE,"E88")])],"isStart":true})});
            var Q1;
            Q1=makeQuery(id+"F39.boolean.opBoolean","COPY",EDGE,{"derivedFrom":makeQuery(id+"F39.opExtrude","CAP_EDGE",EDGE,{"disambiguationData":[OSD([sQuery(id+"F38.wireOp",EDGE,"E87")])],"isStart":true})});
            var Q2;
            Q2=makeQuery(id+"F39.boolean.opBoolean","COPY",EDGE,{"derivedFrom":makeQuery(id+"F39.opExtrude","CAP_EDGE",EDGE,{"disambiguationData":[OSD([sQuery(id+"F38.wireOp",EDGE,"E86")])],"isStart":true})});
            var Q3;
            Q3=makeQuery(id+"F39.boolean.opBoolean","COPY",EDGE,{"derivedFrom":makeQuery(id+"F39.opExtrude","CAP_EDGE",EDGE,{"disambiguationData":[OSD([sQuery(id+"F38.wireOp",EDGE,"E85")])],"isStart":true})});
            var Q4;
            Q4=makeQuery(id+"F39.boolean.opBoolean","COPY",EDGE,{"derivedFrom":makeQuery(id+"F39.opExtrude","CAP_EDGE",EDGE,{"disambiguationData":[OSD([sQuery(id+"F38.wireOp",EDGE,"E84")])],"isStart":true})});
            var Q5;
            Q5=makeQuery(id+"F39.boolean.opBoolean","COPY",EDGE,{"derivedFrom":makeQuery(id+"F39.opExtrude","CAP_EDGE",EDGE,{"disambiguationData":[OSD([sQuery(id+"F38.wireOp",EDGE,"E83")])],"isStart":true})});
            var Q6;
            Q6=makeQuery(id+"F39.boolean.opBoolean","COPY",FACE,{"derivedFrom":makeQuery(id+"F39.opExtrude","SWEPT_FACE",FACE,{"disambiguationData":[OSD([sQuery(id+"F38.wireOp",EDGE,"E84")])]})});
            var Q7;
            Q7=makeQuery(id+"F39.boolean.opBoolean","COPY",FACE,{"derivedFrom":makeQuery(id+"F39.opExtrude","SWEPT_FACE",FACE,{"disambiguationData":[OSD([sQuery(id+"F38.wireOp",EDGE,"E85")])]})});
            var Q8;
            Q8=makeQuery(id+"F39.boolean.opBoolean","COPY",EDGE,{"derivedFrom":makeQuery(id+"F39.opExtrude","SWEPT_EDGE",EDGE,{"disambiguationData":[OSD([sQuery(id+"F0.wireOp",EDGE,"E2"),sQuery(id+"F38.wireOp",EDGE,"E86"),sQuery(id+"F38.wireOp",EDGE,"E87")])]})});
            var Q9;
            Q9=makeQuery(id+"F39.boolean.opBoolean","COPY",FACE,{"derivedFrom":makeQuery(id+"F39.opExtrude","SWEPT_FACE",FACE,{"disambiguationData":[OSD([sQuery(id+"F38.wireOp",EDGE,"E87")])]})});
            var Q10;
            Q10=makeQuery(id+"F39.boolean.opBoolean","COPY",FACE,{"derivedFrom":makeQuery(id+"F39.opExtrude","SWEPT_FACE",FACE,{"disambiguationData":[OSD([sQuery(id+"F38.wireOp",EDGE,"E89")])]})});
            var Q11;
            Q11=makeQuery(id+"F39.boolean.opBoolean","COPY",FACE,{"derivedFrom":makeQuery(id+"F39.opExtrude","SWEPT_FACE",FACE,{"disambiguationData":[OSD([sQuery(id+"F38.wireOp",EDGE,"E90")])]})});
            var Q12;
            Q12=makeQuery(id+"F39.boolean.opBoolean","COPY",FACE,{"derivedFrom":makeQuery(id+"F39.opExtrude","SWEPT_FACE",FACE,{"disambiguationData":[OSD([sQuery(id+"F38.wireOp",EDGE,"E91")])]})});
            var Q13;
            {var subQ0=sQuery(id+"F0.wireOp",EDGE,"E3.top");Q13=makeQuery(id+"F6.boolean.opBoolean","MERGE",FACE,{"derivedFrom":[makeQuery(id+"F1.opExtrude","CAP_FACE",FACE,{"disambiguationData":[OSD([sQuery(id+"F0.wireOp",EDGE,"E1"),sQuery(id+"F0.wireOp",EDGE,"E2"),subQ0,sQuery(id+"F0.wireOp",EDGE,"E3.right"),sQuery(id+"F0.wireOp",EDGE,"E4"),sQuery(id+"F0.wireOp",EDGE,"E5.trimOffspring")])],"isStart":false}),makeQuery(id+"F6.opExtrude","CAP_FACE",FACE,{"disambiguationData":[OSD([subQ0,sQuery(id+"F0.wireOp",EDGE,"E7.top"),sQuery(id+"F0.wireOp",EDGE,"E7.left"),sQuery(id+"F0.wireOp",EDGE,"E7.right"),sQuery(id+"F0.wireOp",EDGE,"E8")])],"isStart":false}),makeQuery(id+"F6.opExtrude","CAP_FACE",FACE,{"disambiguationData":[OSD([subQ0,sQuery(id+"F0.wireOp",EDGE,"E6.top"),sQuery(id+"F0.wireOp",EDGE,"E6.left"),sQuery(id+"F0.wireOp",EDGE,"E6.right"),sQuery(id+"F0.wireOp",EDGE,"E9")])],"isStart":false})]});}
            var Q14;
            Q14=makeQuery(id+"F29.opExtrude","CAP_EDGE",EDGE,{"disambiguationData":[OSD([sQuery(id+"F28.wireOp",EDGE,"E43")])],"isStart":true});
            var Q15;
            Q15=makeQuery(id+"F29.opExtrude","CAP_FACE",FACE,{"disambiguationData":[OSD([sQuery(id+"F28.wireOp",EDGE,"E44")])],"isStart":true});
            var Q16;
            Q16=makeQuery(id+"F29.opExtrude","CAP_FACE",FACE,{"disambiguationData":[OSD([sQuery(id+"F28.wireOp",EDGE,"E45")])],"isStart":true});
            var Q17;
            Q17=makeQuery(id+"F29.opExtrude","CAP_FACE",FACE,{"disambiguationData":[OSD([sQuery(id+"F28.wireOp",EDGE,"E46")])],"isStart":true});
            var Q18;
            Q18=makeQuery(id+"F29.opExtrude","CAP_EDGE",EDGE,{"disambiguationData":[OSD([sQuery(id+"F28.wireOp",EDGE,"E47")])],"isStart":true});
            var Q19;
            Q19=makeQuery(id+"F29.opExtrude","CAP_FACE",FACE,{"disambiguationData":[OSD([sQuery(id+"F28.wireOp",EDGE,"E48")])],"isStart":true});
            var Q20;
            Q20=makeQuery(id+"F29.opExtrude","CAP_FACE",FACE,{"disambiguationData":[OSD([sQuery(id+"F28.wireOp",EDGE,"E42")])],"isStart":true});
            var Q21;
            Q21=makeQuery(id+"F34.opExtrude","CAP_FACE",FACE,{"disambiguationData":[OSD([sQuery(id+"F33.wireOp",EDGE,"E69"),sQuery(id+"F33.wireOp",EDGE,"E70"),sQuery(id+"F33.wireOp",EDGE,"E71"),sQuery(id+"F33.wireOp",EDGE,"E73"),sQuery(id+"F33.wireOp",EDGE,"E74"),sQuery(id+"F33.wireOp",EDGE,"E75")])],"isStart":false});
            var Q22;
            Q22=makeQuery(id+"F34.opExtrude","SWEPT_FACE",FACE,{"disambiguationData":[OSD([sQuery(id+"F33.wireOp",EDGE,"E70")])]});
            var Q23;
            Q23=makeQuery(id+"F34.opExtrude","CAP_FACE",FACE,{"disambiguationData":[OSD([sQuery(id+"F33.wireOp",EDGE,"E69"),sQuery(id+"F33.wireOp",EDGE,"E70"),sQuery(id+"F33.wireOp",EDGE,"E71"),sQuery(id+"F33.wireOp",EDGE,"E73"),sQuery(id+"F33.wireOp",EDGE,"E74"),sQuery(id+"F33.wireOp",EDGE,"E75")])],"isStart":true});
            var Q24;
            Q24=makeQuery(id+"F34.opExtrude","SWEPT_FACE",FACE,{"disambiguationData":[OSD([sQuery(id+"F33.wireOp",EDGE,"E69")])]});
            var Q25;
            Q25=makeQuery(id+"F37.opExtrude","SWEPT_FACE",FACE,{"disambiguationData":[OSD([sQuery(id+"F36.wireOp",EDGE,"E76")])]});
            var Q26;
            Q26=makeQuery(id+"F37.opExtrude","CAP_FACE",FACE,{"disambiguationData":[OSD([sQuery(id+"F36.wireOp",EDGE,"E76"),sQuery(id+"F36.wireOp",EDGE,"E77"),sQuery(id+"F36.wireOp",EDGE,"E79"),sQuery(id+"F36.wireOp",EDGE,"E80"),sQuery(id+"F36.wireOp",EDGE,"E81"),sQuery(id+"F36.wireOp",EDGE,"E82")])],"isStart":false});
            var Q27;
            Q27=makeQuery(id+"F37.opExtrude","SWEPT_FACE",FACE,{"disambiguationData":[OSD([sQuery(id+"F36.wireOp",EDGE,"E77")])]});
            var Q28;
            Q28=makeQuery(id+"F37.opExtrude","CAP_FACE",FACE,{"disambiguationData":[OSD([sQuery(id+"F36.wireOp",EDGE,"E76"),sQuery(id+"F36.wireOp",EDGE,"E77"),sQuery(id+"F36.wireOp",EDGE,"E79"),sQuery(id+"F36.wireOp",EDGE,"E80"),sQuery(id+"F36.wireOp",EDGE,"E81"),sQuery(id+"F36.wireOp",EDGE,"E82")])],"isStart":true});
            var Q29;
            Q29=makeQuery(id+"F31.opExtrude","CAP_FACE",FACE,{"disambiguationData":[OSD([sQuery(id+"F30.wireOp",EDGE,"E50.bottom"),sQuery(id+"F30.wireOp",EDGE,"E50.top"),sQuery(id+"F30.wireOp",EDGE,"E50.left"),sQuery(id+"F30.wireOp",EDGE,"E50.right"),sQuery(id+"F30.wireOp",EDGE,"E60.bottom"),sQuery(id+"F30.wireOp",EDGE,"E60.top"),sQuery(id+"F30.wireOp",EDGE,"E60.left"),sQuery(id+"F30.wireOp",EDGE,"E60.right"),sQuery(id+"F30.wireOp",EDGE,"E61.bottom"),sQuery(id+"F30.wireOp",EDGE,"E61.top"),sQuery(id+"F30.wireOp",EDGE,"E61.left"),sQuery(id+"F30.wireOp",EDGE,"E61.right")])],"isStart":false});
            var Q30;
            Q30=makeQuery(id+"F31.opExtrude","CAP_FACE",FACE,{"disambiguationData":[OSD([sQuery(id+"F30.wireOp",EDGE,"E51.bottom"),sQuery(id+"F30.wireOp",EDGE,"E51.top"),sQuery(id+"F30.wireOp",EDGE,"E51.left"),sQuery(id+"F30.wireOp",EDGE,"E51.right"),sQuery(id+"F30.wireOp",EDGE,"E52.bottom"),sQuery(id+"F30.wireOp",EDGE,"E52.top"),sQuery(id+"F30.wireOp",EDGE,"E52.left"),sQuery(id+"F30.wireOp",EDGE,"E52.right"),sQuery(id+"F30.wireOp",EDGE,"E53.bottom"),sQuery(id+"F30.wireOp",EDGE,"E53.top"),sQuery(id+"F30.wireOp",EDGE,"E53.left"),sQuery(id+"F30.wireOp",EDGE,"E53.right"),sQuery(id+"F30.wireOp",EDGE,"E54.bottom"),sQuery(id+"F30.wireOp",EDGE,"E54.top"),sQuery(id+"F30.wireOp",EDGE,"E54.left"),sQuery(id+"F30.wireOp",EDGE,"E54.right"),sQuery(id+"F30.wireOp",EDGE,"E55.bottom"),sQuery(id+"F30.wireOp",EDGE,"E55.top"),sQuery(id+"F30.wireOp",EDGE,"E55.left"),sQuery(id+"F30.wireOp",EDGE,"E55.right"),sQuery(id+"F30.wireOp",EDGE,"E56.bottom"),sQuery(id+"F30.wireOp",EDGE,"E56.top"),sQuery(id+"F30.wireOp",EDGE,"E56.left"),sQuery(id+"F30.wireOp",EDGE,"E56.right"),sQuery(id+"F30.wireOp",EDGE,"E57.bottom"),sQuery(id+"F30.wireOp",EDGE,"E57.top"),sQuery(id+"F30.wireOp",EDGE,"E57.left"),sQuery(id+"F30.wireOp",EDGE,"E57.right"),sQuery(id+"F30.wireOp",EDGE,"E58"),sQuery(id+"F30.wireOp",EDGE,"E59")])],"isStart":false});
            var Q31;
            {var subQ4=sQuery(id+"F0.wireOp",EDGE,"E3.top");var subQ11=sQuery(id+"F0.wireOp",EDGE,"E3.right");Q31=makeQuery(id+"F31.boolean.opBoolean","SPLIT",FACE,{"disambiguationData":[TD([makeQuery(id+"F1.opExtrude","SWEPT_FACE",FACE,{"disambiguationData":[OSD([subQ4])]})])],"derivedFrom":makeQuery(id+"F1.opExtrude","SWEPT_FACE",FACE,{"disambiguationData":[OSD([subQ11])]})});}
            var Q32;
            Q32=makeQuery(id+"F1.opExtrude","SWEPT_FACE",FACE,{"disambiguationData":[OSD([sQuery(id+"F0.wireOp",EDGE,"E3.top")])]});
            var Q33;
            Q33=makeQuery(id+"F5.opExtrude","CAP_FACE",FACE,{"disambiguationData":[OSD([sQuery(id+"F4.wireOp",EDGE,"E13")])],"isStart":false});
            var Q34;
            Q34=makeQuery(id+"F5.opExtrude","CAP_FACE",FACE,{"disambiguationData":[OSD([sQuery(id+"F4.wireOp",EDGE,"E11")])],"isStart":false});
            var Q35;
            Q35=makeQuery(id+"F5.opExtrude","CAP_FACE",FACE,{"disambiguationData":[OSD([sQuery(id+"F4.wireOp",EDGE,"E10")])],"isStart":false});
            var Q36;
            Q36=makeQuery(id+"F5.opExtrude","CAP_FACE",FACE,{"disambiguationData":[OSD([sQuery(id+"F4.wireOp",EDGE,"E12")])],"isStart":false});
            var Q37;
            Q37=makeQuery(id+"F1.opExtrude","SWEPT_FACE",FACE,{"disambiguationData":[OSD([sQuery(id+"F0.wireOp",EDGE,"E4")])]});
            var Q38;
            Q38=makeQuery(id+"F22.opPattern","COPY",EDGE,{"derivedFrom":makeQuery(id+"F13.opExtrude","CAP_EDGE",EDGE,{"disambiguationData":[OSD([sQuery(id+"F12.wireOp",EDGE,"E18.4")])],"isStart":false}),"instanceName":"1"});
            var Q39;
            Q39=makeQuery(id+"F22.opPattern","COPY",FACE,{"derivedFrom":makeQuery(id+"F13.opExtrude","CAP_FACE",FACE,{"disambiguationData":[OSD([sQuery(id+"F12.wireOp",EDGE,"E18.0"),sQuery(id+"F12.wireOp",EDGE,"E18.1"),sQuery(id+"F12.wireOp",EDGE,"E18.2"),sQuery(id+"F12.wireOp",EDGE,"E18.3"),sQuery(id+"F12.wireOp",EDGE,"E18.4"),sQuery(id+"F12.wireOp",EDGE,"E18.5")])],"isStart":false}),"instanceName":"1"});
            var Q40;
            Q40=makeQuery(id+"F13.opExtrude","CAP_FACE",FACE,{"disambiguationData":[OSD([sQuery(id+"F12.wireOp",EDGE,"E18.0"),sQuery(id+"F12.wireOp",EDGE,"E18.1"),sQuery(id+"F12.wireOp",EDGE,"E18.2"),sQuery(id+"F12.wireOp",EDGE,"E18.3"),sQuery(id+"F12.wireOp",EDGE,"E18.4"),sQuery(id+"F12.wireOp",EDGE,"E18.5")])],"isStart":false});
            var Q41;
            Q41=makeQuery(id+"F22.opPattern","COPY",FACE,{"derivedFrom":makeQuery(id+"F13.opExtrude","CAP_FACE",FACE,{"disambiguationData":[OSD([sQuery(id+"F12.wireOp",EDGE,"E18.0"),sQuery(id+"F12.wireOp",EDGE,"E18.1"),sQuery(id+"F12.wireOp",EDGE,"E18.2"),sQuery(id+"F12.wireOp",EDGE,"E18.3"),sQuery(id+"F12.wireOp",EDGE,"E18.4"),sQuery(id+"F12.wireOp",EDGE,"E18.5")])],"isStart":false}),"instanceName":"7"});
            var Q42;
            Q42=makeQuery(id+"F22.opPattern","COPY",FACE,{"derivedFrom":makeQuery(id+"F13.opExtrude","CAP_FACE",FACE,{"disambiguationData":[OSD([sQuery(id+"F12.wireOp",EDGE,"E18.0"),sQuery(id+"F12.wireOp",EDGE,"E18.1"),sQuery(id+"F12.wireOp",EDGE,"E18.2"),sQuery(id+"F12.wireOp",EDGE,"E18.3"),sQuery(id+"F12.wireOp",EDGE,"E18.4"),sQuery(id+"F12.wireOp",EDGE,"E18.5")])],"isStart":false}),"instanceName":"6"});
            var Q43;
            Q43=makeQuery(id+"F22.opPattern","COPY",FACE,{"derivedFrom":makeQuery(id+"F13.opExtrude","CAP_FACE",FACE,{"disambiguationData":[OSD([sQuery(id+"F12.wireOp",EDGE,"E18.0"),sQuery(id+"F12.wireOp",EDGE,"E18.1"),sQuery(id+"F12.wireOp",EDGE,"E18.2"),sQuery(id+"F12.wireOp",EDGE,"E18.3"),sQuery(id+"F12.wireOp",EDGE,"E18.4"),sQuery(id+"F12.wireOp",EDGE,"E18.5")])],"isStart":false}),"instanceName":"2"});
            var Q44;
            Q44=makeQuery(id+"F22.opPattern","COPY",FACE,{"derivedFrom":makeQuery(id+"F13.opExtrude","CAP_FACE",FACE,{"disambiguationData":[OSD([sQuery(id+"F12.wireOp",EDGE,"E18.0"),sQuery(id+"F12.wireOp",EDGE,"E18.1"),sQuery(id+"F12.wireOp",EDGE,"E18.2"),sQuery(id+"F12.wireOp",EDGE,"E18.3"),sQuery(id+"F12.wireOp",EDGE,"E18.4"),sQuery(id+"F12.wireOp",EDGE,"E18.5")])],"isStart":false}),"instanceName":"3"});
            var Q45;
            Q45=makeQuery(id+"F22.opPattern","COPY",FACE,{"derivedFrom":makeQuery(id+"F13.opExtrude","CAP_FACE",FACE,{"disambiguationData":[OSD([sQuery(id+"F12.wireOp",EDGE,"E18.0"),sQuery(id+"F12.wireOp",EDGE,"E18.1"),sQuery(id+"F12.wireOp",EDGE,"E18.2"),sQuery(id+"F12.wireOp",EDGE,"E18.3"),sQuery(id+"F12.wireOp",EDGE,"E18.4"),sQuery(id+"F12.wireOp",EDGE,"E18.5")])],"isStart":false}),"instanceName":"4"});
            var Q46;
            Q46=makeQuery(id+"F22.opPattern","COPY",FACE,{"derivedFrom":makeQuery(id+"F13.opExtrude","CAP_FACE",FACE,{"disambiguationData":[OSD([sQuery(id+"F12.wireOp",EDGE,"E18.0"),sQuery(id+"F12.wireOp",EDGE,"E18.1"),sQuery(id+"F12.wireOp",EDGE,"E18.2"),sQuery(id+"F12.wireOp",EDGE,"E18.3"),sQuery(id+"F12.wireOp",EDGE,"E18.4"),sQuery(id+"F12.wireOp",EDGE,"E18.5")])],"isStart":false}),"instanceName":"5"});
            var Q47;
            Q47=makeQuery(id+"F29.opExtrude","CAP_FACE",FACE,{"disambiguationData":[OSD([sQuery(id+"F28.wireOp",EDGE,"E49")])],"isStart":true});
            fillet(context, id + "F46", {"entities" : qUnion([Q0, Q1, Q2, Q3, Q4, Q5, Q6, Q7, Q8, Q9, Q10, Q11, Q12, Q13, Q14, Q15, Q16, Q17, Q18, Q19, Q20, Q21, Q22, Q23, Q24, Q25, Q26, Q27, Q28, Q29, Q30, Q31, Q32, Q33, Q34, Q35, Q36, Q37, Q38, Q39, Q40, Q41, Q42, Q43, Q44, Q45, Q46, Q47]), "radius" : .2 * mm, "tangentPropagation" : true, "allowEdgeOverflow" : false});
        }
    });
